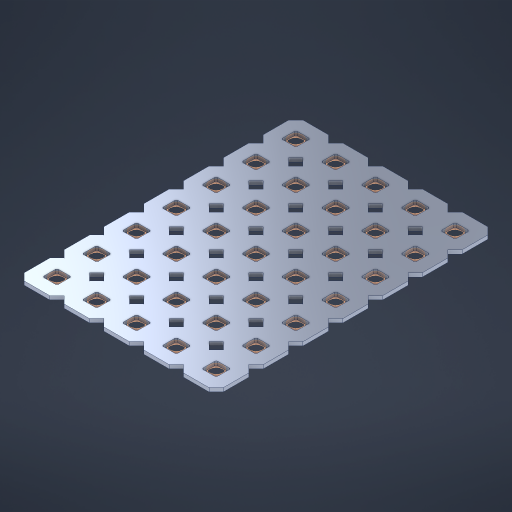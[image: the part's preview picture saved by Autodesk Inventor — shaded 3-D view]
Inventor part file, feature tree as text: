
AUTODESK INVENTOR PART (.ipt)
format: ipt  version: 2023 (Build 270158000, 158)  size: 671,744 bytes
history: native  units: in
note: dims shown in document units (in); Inventor stores cm internally (conversion verified against a paired STEP export)
features: other x36, extrude x34, sketch x2, pattern_linear x1
ambient origin geometry x8: Origin, YZ Plane, XZ Plane, XY Plane, X Axis, Y Axis, Z Axis, Center Point
bodies: Solid1 (feature_tree), Body (feature_tree)
feature tree (73):
  pattern_linear  "Rectangular Pattern1"  Spacing1=0.09in  [1 undecoded]
  sketch  "Sketch1"  dims[d1=0.5in]
  sketch  "Sketch2"  dims[d2=0.182in d3=0.09in d4=0.09in d5=0.09in d6=0.09in d7=0.09in d8=0.09in d9=0.09in d10=0.09in d11=0.02in d13=0.0in d14=0.172in d15=0.0625in d16=0.0in d19=0.5in d22=0.5in]
  other  "Srf1"
  other  "Srf126"
  other  "Srf127"
  other  "Srf128"
  other  "Srf129"
  other  "Srf130"
  other  "Srf131"
  other  "Srf268"
  other  "Srf269"
  other  "Srf270"
  other  "Srf271"
  other  "Srf272"
  other  "Srf273"
  other  "Srf274"
  other  "Srf293"
  other  "Srf294"
  other  "Srf295"
  other  "Srf296"
  other  "Srf297"
  other  "Srf298"
  other  "Srf299"
  other  "Srf318"
  other  "Srf319"
  other  "Srf320"
  other  "Srf321"
  other  "Srf322"
  other  "Srf323"
  other  "Srf324"
  other  "Srf343"
  other  "Srf344"
  other  "Srf345"
  other  "Srf346"
  other  "Srf347"
  other  "Srf348"
  other  "Srf349"
  other  "Circle"
  extrude  "ExtrusionSrf126"  Depth=0.09in
  extrude  "ExtrusionSrf127"  Depth=0.09in
  extrude  "ExtrusionSrf128"  Depth=0.09in
  extrude  "ExtrusionSrf129"  Depth=0.09in
  extrude  "ExtrusionSrf130"  Depth=0.09in
  extrude  "ExtrusionSrf131"  Depth=0.09in
  extrude  "ExtrusionSrf268"  Depth=0.09in
  extrude  "ExtrusionSrf269"  Depth=0.02in
  extrude  "ExtrusionSrf270"  TaperAngle=0.0deg  [1 undecoded]
  extrude  "ExtrusionSrf271"  Depth=0.5in
  extrude  "ExtrusionSrf272"  Depth=0.5in TaperAngle=0.0deg
  extrude  "ExtrusionSrf273"  Depth=0.5in
  extrude  "ExtrusionSrf274"  Depth=0.5in
  extrude  "ExtrusionSrf293"  [1 undecoded]
  extrude  "ExtrusionSrf294"  [1 undecoded]
  extrude  "ExtrusionSrf295"  [1 undecoded]
  extrude  "ExtrusionSrf296"  [1 undecoded]
  extrude  "ExtrusionSrf297"  [1 undecoded]
  extrude  "ExtrusionSrf298"  [1 undecoded]
  extrude  "ExtrusionSrf299"  [1 undecoded]
  extrude  "ExtrusionSrf318"  [1 undecoded]
  extrude  "ExtrusionSrf319"  [1 undecoded]
  extrude  "ExtrusionSrf320"  [1 undecoded]
  extrude  "ExtrusionSrf321"  [1 undecoded]
  extrude  "ExtrusionSrf322"  [1 undecoded]
  extrude  "ExtrusionSrf323"  [1 undecoded]
  extrude  "ExtrusionSrf324"  [1 undecoded]
  extrude  "ExtrusionSrf343"  [1 undecoded]
  extrude  "ExtrusionSrf344"  [1 undecoded]
  extrude  "ExtrusionSrf345"  [1 undecoded]
  extrude  "ExtrusionSrf346"  [1 undecoded]
  extrude  "ExtrusionSrf347"  [1 undecoded]
  extrude  "ExtrusionSrf348"  [1 undecoded]
  extrude  "ExtrusionSrf349"  [1 undecoded]
note: 23 required parameter values undecoded (feature->parameter linkage not recoverable at this tier; creation-order binding heuristic only, values carry confidence <= 0.55)
